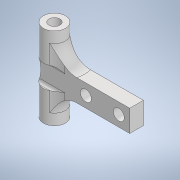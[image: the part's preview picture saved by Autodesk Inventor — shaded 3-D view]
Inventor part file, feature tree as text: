
AUTODESK INVENTOR PART (.ipt)
format: ipt  version: 2020 (Build 240168000, 168)  size: 304,640 bytes
history: native  units: mm
features: extrude x7, sketch x7, projected_geometry x5, fillet x4, other x3, reference x1
ambient origin geometry x8: Origin, YZ Plane, XZ Plane, XY Plane, X Axis, Y Axis, Z Axis, Center Point
bodies: Solid1 (feature_tree)
feature tree (27):
  extrude  "Extrusion1"  Depth=20.0mm
  extrude  "Extrusion2"  Depth=10.0mm
  extrude  "Extrusion3"  Depth=5.0mm TaperAngle=0.0deg
  extrude  "Extrusion4"  Depth=4.0mm
  fillet  "Fillet1"  Radius=5.0mm
  fillet  "Fillet2"  Radius=4.0mm
  fillet  "Fillet3"  Radius=8.0mm
  fillet  "Fillet4"  Radius=5.0mm
  extrude  "Extrusion5"  Depth=5.0mm
  extrude  "Extrusion6"  Depth=7.0mm
  extrude  "Extrusion7"  Depth=4.0mm
  sketch  "Sketch1"  dims[d0=20.0mm d1=8.0mm]
  reference  "Reference1"
  sketch  "Sketch2"  dims[d2=10.0mm d3=30.0mm]
  projected_geometry  "Projected Loop1"
  sketch  "Sketch3"  dims[d4=5.0mm d5=5.0mm d6=0.0mm]
  projected_geometry  "Projected Loop2"
  sketch  "Sketch4"  dims[d7=4.0mm d8=4.0mm d9=5.0mm d10=0.0mm d11=4.0mm d12=8.0mm d13=5.0mm d14=0.0mm]
  projected_geometry  "Projected Loop3"
  sketch  "Sketch5"  dims[d15=5.0mm d16=0.0mm d17=6.0mm]
  projected_geometry  "Projected Loop4"
  sketch  "Sketch6"  dims[d18=1.0mm d19=7.0mm]
  sketch  "Sketch7"  dims[d20=10.0mm d21=4.0mm d22=5.0mm d23=0.0mm d24=5.0mm d25=0.0mm d26=2.5mm d27=25.0mm d28=0.0mm]
  projected_geometry  "Projected Loop5"
  parser-record x1  (decoder bookkeeping rows leaked as tree rows — omitted from the tree; the rows remain in map.json)
  other  "delta_1.iam"
  other  "arm_2:5"
note: 1 file-system path scrubbed to <path> (originals preserved in map.json)
